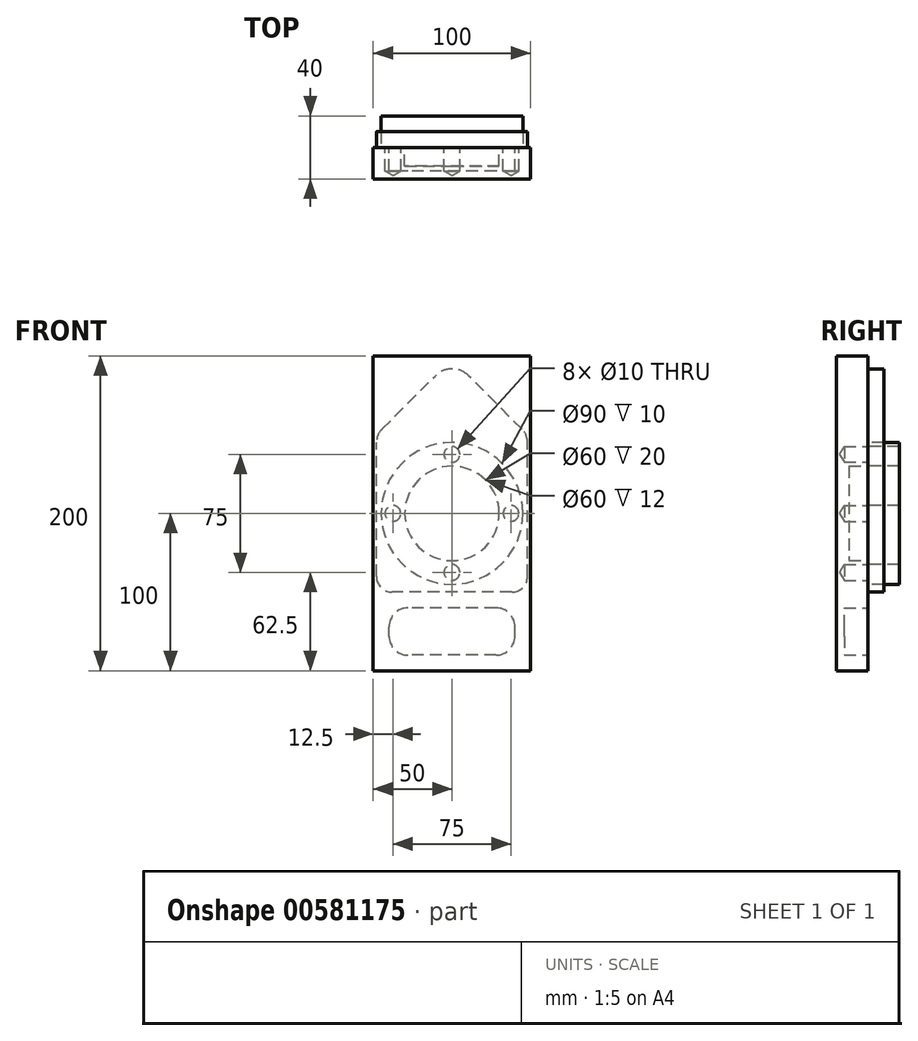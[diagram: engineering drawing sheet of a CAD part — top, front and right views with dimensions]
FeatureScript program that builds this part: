
annotation { "Feature Type Name" : "Feature", "Feature Type Description" : "" }
export const myFeature = defineFeature(function(context is Context, id is Id, definition is map)
    precondition{}
    {
        {
            var Q0;
            Q0=qCreatedBy(makeId("Front.planeOp"),FACE);
            var sketch = newSketch(context, id + "F0", { "sketchPlane" : qUnion([Q0])});
            skLineSegment(sketch, "E0.bottom", {"start": v(50, -100) * mm, "end": v(-50, -100) * mm});
            skLineSegment(sketch, "E0.top", {"start": v(50, 100) * mm, "end": v(-50, 100) * mm});
            skLineSegment(sketch, "E0.left", {"start": v(50, -100) * mm, "end": v(50, 100) * mm});
            skLineSegment(sketch, "E0.right", {"start": v(-50, -100) * mm, "end": v(-50, 100) * mm});
            skLineSegment(sketch, "E1", {"start": v(0, -100) * mm, "end": v(0, 0) * mm, "construction": true});
            skPoint(sketch, "E1.endSnap0", {"position": v(0, -100) * mm});
            skLineSegment(sketch, "E2", {"start": v(0, 0) * mm, "end": v(50, 0) * mm, "construction": true});
            skSolve(sketch);
        }
        {
            var Q0;
            Q0=makeQuery(id+"F0.imprint","IMPRINT",FACE,{"disambiguationData":[TD([[makeQuery(id+"F0.imprint","IMPRINT",EDGE,{"derivedFrom":sQuery(id+"F0.wireOp",EDGE,"E0.bottom")}),-1.0]])]});
            extrude(context, id + "F1", {"entities" : qUnion([Q0]), "depth" : 20 * mm, "offsetDistance" : 25 * mm});
        }
        {
            var Q0;
            Q0=makeQuery(id+"F1.opExtrude","CAP_FACE",FACE,{"disambiguationData":[OSD([sQuery(id+"F0.wireOp",EDGE,"E0.bottom"),sQuery(id+"F0.wireOp",EDGE,"E0.top"),sQuery(id+"F0.wireOp",EDGE,"E0.left"),sQuery(id+"F0.wireOp",EDGE,"E0.right")])],"isStart":true});
            var sketch = newSketch(context, id + "F2", { "sketchPlane" : qUnion([Q0])});
            skLineSegment(sketch, "E3.bottom", {"start": v(-28, -90) * mm, "end": v(28, -90) * mm});
            skLineSegment(sketch, "E3.top", {"start": v(-28, -60) * mm, "end": v(28, -60) * mm});
            skLineSegment(sketch, "E3.left", {"start": v(-40, -78) * mm, "end": v(-40, -72) * mm});
            skLineSegment(sketch, "E3.right", {"start": v(40, -78) * mm, "end": v(40, -72) * mm});
            skLineSegment(sketch, "E4", {"start": v(-38, -50) * mm, "end": v(38, -50) * mm});
            skLineSegment(sketch, "E5", {"start": v(-48, -40) * mm, "end": v(-48, 45.03) * mm});
            skLineSegment(sketch, "E6", {"start": v(48, -40) * mm, "end": v(48, 45.03) * mm});
            skArc(sketch, "E7", {"start": v(-48, -40) * mm, "mid": v(-45.07, -47.07) * mm, "end": v(-38, -50) * mm});
            skArc(sketch, "E8", {"start": v(38, -50) * mm, "mid": v(45.07, -47.07) * mm, "end": v(48, -40) * mm});
            skArc(sketch, "E9", {"start": v(-40, -78) * mm, "mid": v(-36.49, -86.49) * mm, "end": v(-28, -90) * mm});
            skArc(sketch, "E10", {"start": v(-28, -60) * mm, "mid": v(-36.49, -63.51) * mm, "end": v(-40, -72) * mm});
            skArc(sketch, "E11", {"start": v(28, -90) * mm, "mid": v(36.49, -86.49) * mm, "end": v(40, -78) * mm});
            skArc(sketch, "E12", {"start": v(40, -72) * mm, "mid": v(36.49, -63.51) * mm, "end": v(28, -60) * mm});
            skLineSegment(sketch, "E13", {"start": v(0, -100) * mm, "end": v(0, 100) * mm, "construction": true});
            skLineSegment(sketch, "E14", {"start": v(-50, 0) * mm, "end": v(50, 0) * mm, "construction": true});
            skCircle(sketch, "E15", {"center": v(0, 0) * mm, "radius": 45 * mm});
            skCircle(sketch, "E16", {"center": v(0, 0) * mm, "radius": 30 * mm});
            skLineSegment(sketch, "E17", {"start": v(-44.49, 53.51) * mm, "end": v(-10.6, 87.4) * mm});
            skLineSegment(sketch, "E18", {"start": v(44.49, 53.51) * mm, "end": v(10.6, 87.4) * mm});
            skArc(sketch, "E19", {"start": v(-44.49, 53.51) * mm, "mid": v(-47.09, 49.62) * mm, "end": v(-48, 45.03) * mm});
            skArc(sketch, "E20", {"start": v(48, 45.03) * mm, "mid": v(47.09, 49.62) * mm, "end": v(44.49, 53.51) * mm});
            skArc(sketch, "E21", {"start": v(10.6, 87.4) * mm, "mid": v(0, 91.79) * mm, "end": v(-10.6, 87.4) * mm});
            skCircle(sketch, "E22", {"center": v(0, 0) * mm, "radius": 37.5 * mm, "construction": true});
            skCircle(sketch, "E23", {"center": v(-37.5, 0) * mm, "radius": 5 * mm});
            skCircle(sketch, "E24", {"center": v(0, 37.5) * mm, "radius": 5 * mm});
            skCircle(sketch, "E25", {"center": v(37.5, 0) * mm, "radius": 5 * mm});
            skCircle(sketch, "E26", {"center": v(0, -37.5) * mm, "radius": 5 * mm});
            skSolve(sketch);
        }
        {
            var Q0;
            Q0=makeQuery(id+"F2.imprint","IMPRINT",FACE,{"disambiguationData":[TD([[makeQuery(id+"F2.imprint","IMPRINT",EDGE,{"derivedFrom":sQuery(id+"F2.wireOp",EDGE,"E3.bottom")}),1.0]])]});
            extrude(context, id + "F3", {"entities" : qUnion([Q0]), "operationType" : NewBodyOperationType.REMOVE, "oppositeDirection" : true, "depth" : 15 * mm, "offsetDistance" : 25 * mm});
        }
        {
            var Q0;
            Q0=makeQuery(id+"F2.imprint","IMPRINT",FACE,{"disambiguationData":[TD([[makeQuery(id+"F2.imprint","IMPRINT",EDGE,{"derivedFrom":sQuery(id+"F2.wireOp",EDGE,"E4")}),1.0]])]});
            extrude(context, id + "F4", {"entities" : qUnion([Q0]), "depth" : 10 * mm, "offsetDistance" : 25 * mm});
        }
        {
            var Q0;
            Q0=makeQuery(id+"F2.imprint","IMPRINT",FACE,{"disambiguationData":[TD([[makeQuery(id+"F2.imprint","IMPRINT",EDGE,{"derivedFrom":sQuery(id+"F2.wireOp",EDGE,"E15")}),1.0]])]});
            extrude(context, id + "F5", {"entities" : qUnion([Q0]), "depth" : 20 * mm, "offsetDistance" : 25 * mm});
        }
        {
            var Q0;
            Q0=sQuery(id+"F2.wireOp",VERTEX,"E23.center");
            var Q1;
            Q1=sQuery(id+"F2.wireOp",VERTEX,"E26.center");
            var Q2;
            Q2=sQuery(id+"F2.wireOp",VERTEX,"E25.center");
            var Q3;
            Q3=sQuery(id+"F2.wireOp",VERTEX,"E24.center");
            var Q4;
            Q4=makeQuery(id+"F1.opExtrude","SWEPT_BODY",BODY,{"disambiguationData":[OSD([sQuery(id+"F0.wireOp",EDGE,"E0.bottom"),sQuery(id+"F0.wireOp",EDGE,"E0.top"),sQuery(id+"F0.wireOp",EDGE,"E0.left"),sQuery(id+"F0.wireOp",EDGE,"E0.right")])]});
            hole(context, id + "F6", {"style" : HoleStyle.SIMPLE, "endStyle" : HoleEndStyle.BLIND, "holeDiameter" : 10 * mm, "majorDiameter" : 5 * mm, "holeDepth" : 15 * mm, "isTappedThrough" : true, "tappedDepth" : 12 * mm, "tapClearance" : 3, "locations" : qUnion([Q0, Q1, Q2, Q3]), "scope" : qUnion([Q4])});
        }
        {
            var Q0;
            Q0=makeQuery(id+"F2.imprint","IMPRINT",FACE,{"disambiguationData":[TD([[makeQuery(id+"F2.imprint","IMPRINT",EDGE,{"derivedFrom":sQuery(id+"F2.wireOp",EDGE,"E16")}),1.0]])]});
            extrude(context, id + "F7", {"entities" : qUnion([Q0]), "operationType" : NewBodyOperationType.REMOVE, "oppositeDirection" : true, "depth" : 12 * mm, "offsetDistance" : 25 * mm});
        }
    });
